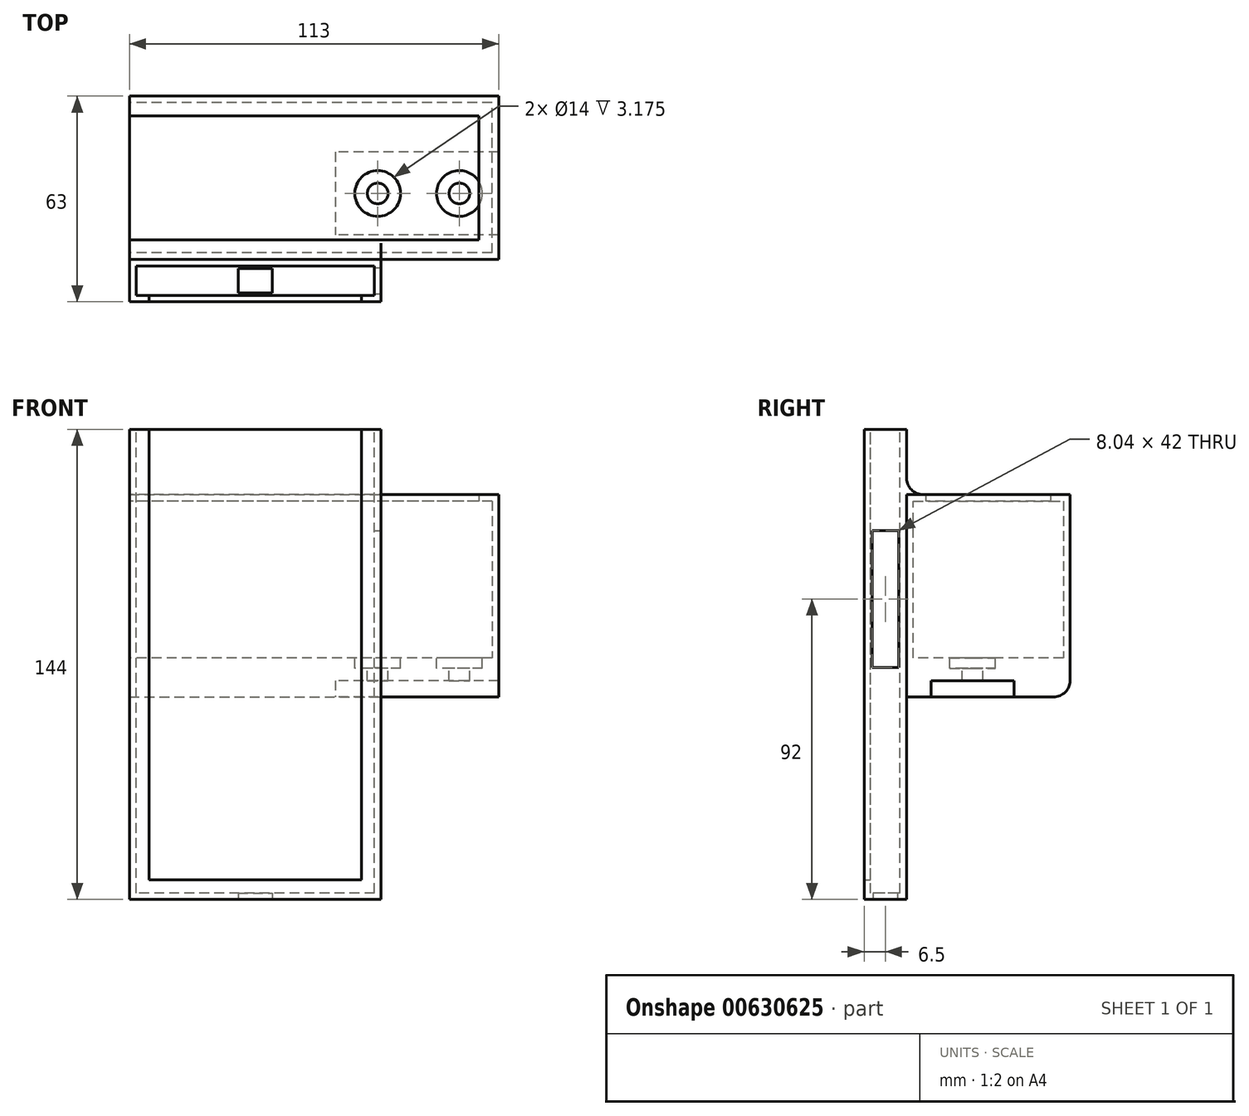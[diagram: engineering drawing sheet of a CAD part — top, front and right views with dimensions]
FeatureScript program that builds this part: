
annotation { "Feature Type Name" : "Feature", "Feature Type Description" : "" }
export const myFeature = defineFeature(function(context is Context, id is Id, definition is map)
    precondition{}
    {
        {
            var Q0;
            Q0=qCreatedBy(makeId("Front.planeOp"),FACE);
            var sketch = newSketch(context, id + "F0", { "sketchPlane" : qUnion([Q0])});
            skLineSegment(sketch, "E0.bottom", {"start": v(38.5, -72) * mm, "end": v(-38.5, -72) * mm});
            skLineSegment(sketch, "E0.top", {"start": v(38.5, 72) * mm, "end": v(-38.5, 72) * mm});
            skLineSegment(sketch, "E0.left", {"start": v(38.5, -72) * mm, "end": v(38.5, 72) * mm});
            skLineSegment(sketch, "E0.right", {"start": v(-38.5, -72) * mm, "end": v(-38.5, 72) * mm});
            skPoint(sketch, "E0.middle", {"position": v(0, 0) * mm});
            skSolve(sketch);
        }
        {
            var Q0;
            Q0=makeQuery(id+"F0.imprint","IMPRINT",FACE,{"disambiguationData":[TD([[makeQuery(id+"F0.imprint","IMPRINT",EDGE,{"derivedFrom":sQuery(id+"F0.wireOp",EDGE,"E0.bottom")}),-1.0]])]});
            extrude(context, id + "F1", {"entities" : qUnion([Q0]), "depth" : 13 * mm, "offsetDistance" : 25 * mm});
        }
        {
            var Q0;
            Q0=makeQuery(id+"F1.opExtrude","SWEPT_FACE",FACE,{"disambiguationData":[OSD([sQuery(id+"F0.wireOp",EDGE,"E0.top")])]});
            var sketch = newSketch(context, id + "F2", { "sketchPlane" : qUnion([Q0])});
            skLineSegment(sketch, "E1", {"start": v(-32.5, -13) * mm, "end": v(-32.5, -11) * mm});
            skLineSegment(sketch, "E2", {"start": v(-32.5, -11) * mm, "end": v(-36.5, -11) * mm});
            skLineSegment(sketch, "E3", {"start": v(-36.5, -11) * mm, "end": v(-36.5, -2) * mm});
            skLineSegment(sketch, "E4", {"start": v(-36.5, -2) * mm, "end": v(36.5, -2) * mm});
            skLineSegment(sketch, "E5", {"start": v(36.5, -2) * mm, "end": v(36.5, -11) * mm});
            skLineSegment(sketch, "E6", {"start": v(36.5, -11) * mm, "end": v(32.5, -11) * mm});
            skLineSegment(sketch, "E7", {"start": v(32.5, -11) * mm, "end": v(32.5, -13) * mm});
            skSolve(sketch);
        }
        {
            var Q0;
            {var subQ0=sQuery(id+"F2.wireOp",EDGE,"E1");Q0=makeQuery(id+"F2.imprint","IMPRINT",FACE,{"disambiguationData":[TD([[makeQuery(id+"F2.imprint","IMPRINT",EDGE,{"derivedFrom":subQ0}),-1.0]])]});}
            extrude(context, id + "F3", {"entities" : qUnion([Q0]), "operationType" : NewBodyOperationType.REMOVE, "oppositeDirection" : true, "depth" : 142 * mm, "offsetDistance" : 25 * mm});
        }
        {
            var Q0;
            Q0=makeQuery(id+"F3.boolean.opBoolean","COPY",FACE,{"derivedFrom":makeQuery(id+"F3.opExtrude","CAP_FACE",FACE,{"disambiguationData":[OSD([sQuery(id+"F0.wireOp",EDGE,"E0.top"),sQuery(id+"F2.wireOp",EDGE,"E1"),sQuery(id+"F2.wireOp",EDGE,"E2"),sQuery(id+"F2.wireOp",EDGE,"E3"),sQuery(id+"F2.wireOp",EDGE,"E4"),sQuery(id+"F2.wireOp",EDGE,"E5"),sQuery(id+"F2.wireOp",EDGE,"E6"),sQuery(id+"F2.wireOp",EDGE,"E7")])],"isStart":false})});
            var sketch = newSketch(context, id + "F4", { "sketchPlane" : qUnion([Q0])});
            skLineSegment(sketch, "E8", {"start": v(-32.5, -11) * mm, "end": v(32.5, -11) * mm});
            skSolve(sketch);
        }
        {
            var Q0;
            Q0=makeQuery(id+"F4.imprint","IMPRINT",FACE,{"disambiguationData":[TD([[makeQuery(id+"F4.imprint","IMPRINT",EDGE,{"derivedFrom":sQuery(id+"F4.wireOp",EDGE,"E8")}),-1.0]])]});
            extrude(context, id + "F5", {"entities" : qUnion([Q0]), "operationType" : NewBodyOperationType.ADD, "depth" : 4 * mm, "offsetDistance" : 25 * mm});
        }
        {
            var Q0;
            Q0=makeQuery(id+"F1.opExtrude","SWEPT_FACE",FACE,{"disambiguationData":[OSD([sQuery(id+"F0.wireOp",EDGE,"E0.bottom")])]});
            var sketch = newSketch(context, id + "F6", { "sketchPlane" : qUnion([Q0])});
            skPoint(sketch, "E9", {"position": v(0, 6.5) * mm});
            skLineSegment(sketch, "E10.bottom", {"start": v(5.25, 10.25) * mm, "end": v(-5.25, 10.25) * mm});
            skLineSegment(sketch, "E10.top", {"start": v(5.25, 2.75) * mm, "end": v(-5.25, 2.75) * mm});
            skLineSegment(sketch, "E10.left", {"start": v(5.25, 10.25) * mm, "end": v(5.25, 2.75) * mm});
            skLineSegment(sketch, "E10.right", {"start": v(-5.25, 10.25) * mm, "end": v(-5.25, 2.75) * mm});
            skSolve(sketch);
        }
        {
            var Q0;
            Q0=makeQuery(id+"F6.imprint","IMPRINT",FACE,{"disambiguationData":[TD([[makeQuery(id+"F6.imprint","IMPRINT",EDGE,{"derivedFrom":sQuery(id+"F6.wireOp",EDGE,"E10.bottom")}),1.0]])]});
            extrude(context, id + "F7", {"entities" : qUnion([Q0]), "operationType" : NewBodyOperationType.REMOVE, "oppositeDirection" : true, "depth" : 25 * mm, "offsetDistance" : 25 * mm});
        }
        {
            var Q0;
            Q0=makeQuery(id+"F1.opExtrude","SWEPT_FACE",FACE,{"disambiguationData":[OSD([sQuery(id+"F0.wireOp",EDGE,"E0.left")])]});
            var sketch = newSketch(context, id + "F8", { "sketchPlane" : qUnion([Q0])});
            skPoint(sketch, "E11", {"position": v(-6.5, 20) * mm});
            skLineSegment(sketch, "E12.bottom", {"start": v(-2.48, 41) * mm, "end": v(-10.52, 41) * mm});
            skLineSegment(sketch, "E12.top", {"start": v(-2.48, -1) * mm, "end": v(-10.52, -1) * mm});
            skLineSegment(sketch, "E12.left", {"start": v(-2.48, 41) * mm, "end": v(-2.48, -1) * mm});
            skLineSegment(sketch, "E12.right", {"start": v(-10.52, 41) * mm, "end": v(-10.52, -1) * mm});
            skSolve(sketch);
        }
        {
            var Q0;
            Q0=makeQuery(id+"F8.imprint","IMPRINT",FACE,{"disambiguationData":[TD([[makeQuery(id+"F8.imprint","IMPRINT",EDGE,{"derivedFrom":sQuery(id+"F8.wireOp",EDGE,"E12.bottom")}),1.0]])]});
            extrude(context, id + "F9", {"entities" : qUnion([Q0]), "operationType" : NewBodyOperationType.REMOVE, "oppositeDirection" : true, "depth" : 25 * mm, "offsetDistance" : 25 * mm});
        }
        {
            var Q0;
            Q0=makeQuery(id+"F1.opExtrude","CAP_FACE",FACE,{"disambiguationData":[OSD([sQuery(id+"F0.wireOp",EDGE,"E0.bottom"),sQuery(id+"F0.wireOp",EDGE,"E0.top"),sQuery(id+"F0.wireOp",EDGE,"E0.left"),sQuery(id+"F0.wireOp",EDGE,"E0.right")])],"isStart":true});
            var sketch = newSketch(context, id + "F10", { "sketchPlane" : qUnion([Q0])});
            skLineSegment(sketch, "E13.bottom", {"start": v(38.5, 52) * mm, "end": v(-74.5, 52) * mm});
            skLineSegment(sketch, "E13.top", {"start": v(38.5, -2) * mm, "end": v(-74.5, -2) * mm});
            skLineSegment(sketch, "E13.left", {"start": v(38.5, 52) * mm, "end": v(38.5, -2) * mm});
            skLineSegment(sketch, "E13.right", {"start": v(-74.5, 52) * mm, "end": v(-74.5, -2) * mm});
            skSolve(sketch);
        }
        {
            var Q0;
            {var subQ0=sQuery(id+"F10.wireOp",EDGE,"E13.left");Q0=makeQuery(id+"F10.imprint","IMPRINT",FACE,{"disambiguationData":[TD([[makeQuery(id+"F10.imprint","IMPRINT",EDGE,{"derivedFrom":subQ0}),1.0]])]});}
            var Q1;
            {var subQ0=sQuery(id+"F10.wireOp",EDGE,"E13.right");Q1=makeQuery(id+"F10.imprint","IMPRINT",FACE,{"disambiguationData":[TD([[makeQuery(id+"F10.imprint","IMPRINT",EDGE,{"derivedFrom":subQ0}),1.0]])]});}
            extrude(context, id + "F11", {"entities" : qUnion([Q0, Q1]), "operationType" : NewBodyOperationType.ADD, "depth" : 50 * mm, "offsetDistance" : 25 * mm});
        }
        {
            var Q0;
            Q0=makeQuery(id+"F11.boolean.opBoolean","MERGE",FACE,{"derivedFrom":[makeQuery(id+"F1.opExtrude","SWEPT_FACE",FACE,{"disambiguationData":[OSD([sQuery(id+"F0.wireOp",EDGE,"E0.right")])]}),makeQuery(id+"F11.opExtrude","SWEPT_FACE",FACE,{"disambiguationData":[OSD([sQuery(id+"F10.wireOp",EDGE,"E13.left")])]})]});
            var sketch = newSketch(context, id + "F12", { "sketchPlane" : qUnion([Q0])});
            skLineSegment(sketch, "E14", {"start": v(0, 52) * mm, "end": v(0, -2) * mm});
            skLineSegment(sketch, "E15", {"start": v(-44, 52) * mm, "end": v(-44, 50) * mm});
            skLineSegment(sketch, "E16", {"start": v(-44, 50) * mm, "end": v(-48, 50) * mm});
            skLineSegment(sketch, "E17", {"start": v(-48, 50) * mm, "end": v(-48, 2) * mm});
            skLineSegment(sketch, "E18", {"start": v(-48, 2) * mm, "end": v(-2, 2) * mm});
            skLineSegment(sketch, "E19", {"start": v(-2, 2) * mm, "end": v(-2, 50) * mm});
            skLineSegment(sketch, "E20", {"start": v(-2, 50) * mm, "end": v(-6, 50) * mm});
            skLineSegment(sketch, "E21", {"start": v(-6, 50) * mm, "end": v(-6, 52) * mm});
            skSolve(sketch);
        }
        {
            var Q0;
            {var subQ0=sQuery(id+"F12.wireOp",EDGE,"E15");Q0=makeQuery(id+"F12.imprint","IMPRINT",FACE,{"disambiguationData":[TD([[makeQuery(id+"F12.imprint","IMPRINT",EDGE,{"derivedFrom":subQ0}),1.0]])]});}
            extrude(context, id + "F13", {"entities" : qUnion([Q0]), "operationType" : NewBodyOperationType.REMOVE, "oppositeDirection" : true, "depth" : 111 * mm, "offsetDistance" : 25 * mm});
        }
        {
            var Q0;
            Q0=makeQuery(id+"F13.boolean.opBoolean","COPY",FACE,{"derivedFrom":makeQuery(id+"F13.opExtrude","CAP_FACE",FACE,{"disambiguationData":[OSD([sQuery(id+"F0.wireOp",EDGE,"E0.right"),sQuery(id+"F10.wireOp",EDGE,"E13.bottom"),sQuery(id+"F10.wireOp",EDGE,"E13.left"),sQuery(id+"F12.wireOp",EDGE,"E15"),sQuery(id+"F12.wireOp",EDGE,"E16"),sQuery(id+"F12.wireOp",EDGE,"E17"),sQuery(id+"F12.wireOp",EDGE,"E18"),sQuery(id+"F12.wireOp",EDGE,"E19"),sQuery(id+"F12.wireOp",EDGE,"E20"),sQuery(id+"F12.wireOp",EDGE,"E21")])],"isStart":false})});
            var sketch = newSketch(context, id + "F14", { "sketchPlane" : qUnion([Q0])});
            skLineSegment(sketch, "E22", {"start": v(-44, 50) * mm, "end": v(-6, 50) * mm});
            skSolve(sketch);
        }
        {
            var Q0;
            Q0 = qSketchRegion(id + "F14", true);
            var Q1;
            Q1=makeQuery(id+"F14.imprint","IMPRINT",FACE,{"disambiguationData":[TD([[makeQuery(id+"F14.imprint","IMPRINT",EDGE,{"derivedFrom":sQuery(id+"F14.wireOp",EDGE,"E22")}),1.0]])]});
            extrude(context, id + "F15", {"entities" : qUnion([Q0, Q1]), "operationType" : NewBodyOperationType.ADD, "depth" : 4 * mm, "offsetDistance" : 25 * mm});
        }
        {
            var Q0;
            Q0=makeQuery(id+"F11.opExtrude","SWEPT_FACE",FACE,{"disambiguationData":[OSD([sQuery(id+"F10.wireOp",EDGE,"E13.top")])]});
            extrude(context, id + "F16", {"entities" : qUnion([Q0]), "operationType" : NewBodyOperationType.ADD, "depth" : 8 * mm, "offsetDistance" : 25 * mm});
        }
        {
            var Q0;
            Q0=makeQuery(id+"F16.opExtrude","CAP_FACE",FACE,{"disambiguationData":[OSD([sQuery(id+"F10.wireOp",EDGE,"E13.top")])],"isStart":false});
            var sketch = newSketch(context, id + "F17", { "sketchPlane" : qUnion([Q0])});
            skLineSegment(sketch, "E23.bottom", {"start": v(74.5, -32.9) * mm, "end": v(24.5, -32.9) * mm});
            skLineSegment(sketch, "E23.top", {"start": v(74.5, -7.5) * mm, "end": v(24.5, -7.5) * mm});
            skLineSegment(sketch, "E23.left", {"start": v(74.5, -32.9) * mm, "end": v(74.5, -7.5) * mm});
            skLineSegment(sketch, "E23.right", {"start": v(24.5, -32.9) * mm, "end": v(24.5, -7.5) * mm});
            skSolve(sketch);
        }
        {
            var Q0;
            Q0=makeQuery(id+"F17.imprint","IMPRINT",FACE,{"disambiguationData":[TD([[makeQuery(id+"F17.imprint","IMPRINT",EDGE,{"derivedFrom":sQuery(id+"F17.wireOp",EDGE,"E23.bottom")}),-1.0]])]});
            extrude(context, id + "F18", {"entities" : qUnion([Q0]), "operationType" : NewBodyOperationType.REMOVE, "oppositeDirection" : true, "depth" : 5 * mm, "offsetDistance" : 25 * mm});
        }
        {
            var Q0;
            Q0=makeQuery(id+"F13.boolean.opBoolean","COPY",FACE,{"derivedFrom":makeQuery(id+"F13.opExtrude","SWEPT_FACE",FACE,{"disambiguationData":[OSD([sQuery(id+"F12.wireOp",EDGE,"E18")])]})});
            var sketch = newSketch(context, id + "F19", { "sketchPlane" : qUnion([Q0])});
            skPoint(sketch, "E24", {"position": v(62.5, 20.2) * mm});
            skPoint(sketch, "E25", {"position": v(37.5, 20.2) * mm});
            skSolve(sketch);
        }
        {
            var Q0;
            Q0=sQuery(id+"F19.wireOp",VERTEX,"E24");
            var Q1;
            Q1=sQuery(id+"F19.wireOp",VERTEX,"E25");
            var Q2;
            Q2=makeQuery(id+"F1.opExtrude","SWEPT_BODY",BODY,{"disambiguationData":[OSD([sQuery(id+"F0.wireOp",EDGE,"E0.bottom"),sQuery(id+"F0.wireOp",EDGE,"E0.top"),sQuery(id+"F0.wireOp",EDGE,"E0.left"),sQuery(id+"F0.wireOp",EDGE,"E0.right")])]});
            hole(context, id + "F20", {"style" : HoleStyle.C_BORE, "endStyle" : HoleEndStyle.BLIND, "holeDiameter" : 6.35 * mm, "cBoreDiameter" : 14 * mm, "cBoreDepth" : 3.17 * mm, "majorDiameter" : 5 * mm, "holeDepth" : 8 * mm, "isTappedThrough" : true, "tappedDepth" : 12 * mm, "tapClearance" : 3, "locations" : qUnion([Q0, Q1]), "scope" : qUnion([Q2])});
        }
        {
            var Q0;
            {var subQ0=makeQuery(id+"F1.opExtrude","CAP_FACE",FACE,{"disambiguationData":[OSD([sQuery(id+"F0.wireOp",EDGE,"E0.bottom"),sQuery(id+"F0.wireOp",EDGE,"E0.top"),sQuery(id+"F0.wireOp",EDGE,"E0.left"),sQuery(id+"F0.wireOp",EDGE,"E0.right")])],"isStart":true});var subQ1=sQuery(id+"F10.wireOp",EDGE,"E13.top");var subQ3=makeQuery(id+"F11.opExtrude","CAP_EDGE",EDGE,{"disambiguationData":[OSD([subQ1])],"isStart":true});Q0=makeQuery(id+"F16.boolean.opBoolean","SPLIT",EDGE,{"disambiguationData":[topologyDisambiguationEdgeConnected([subQ0])],"derivedFrom":makeQuery(id+"F16.opExtrude","CAP_EDGE",EDGE,{"disambiguationData":[OSD([subQ1]),TDD([makeQuery(id+"F11.boolean.opBoolean","SPLIT",EDGE,{"disambiguationData":[topologyDisambiguationEdgeConnected([makeQuery(id+"F11.opExtrude","CAP_FACE",FACE,{"disambiguationData":[OSD([sQuery(id+"F10.wireOp",EDGE,"E13.bottom"),subQ1,sQuery(id+"F10.wireOp",EDGE,"E13.left"),sQuery(id+"F10.wireOp",EDGE,"E13.right")])],"isStart":true})])],"derivedFrom":subQ3}),makeQuery(id+"F11.boolean.opBoolean","SPLIT",EDGE,{"disambiguationData":[topologyDisambiguationEdgeConnected([subQ0])],"derivedFrom":subQ3})])],"isStart":false})});}
            var Q1;
            {var subQ0=sQuery(id+"F10.wireOp",EDGE,"E13.bottom");Q1=makeQuery(id+"F11.boolean.opBoolean","SPLIT",EDGE,{"disambiguationData":[topologyDisambiguationEdgeConnected([makeQuery(id+"F1.opExtrude","CAP_FACE",FACE,{"disambiguationData":[OSD([sQuery(id+"F0.wireOp",EDGE,"E0.bottom"),sQuery(id+"F0.wireOp",EDGE,"E0.top"),sQuery(id+"F0.wireOp",EDGE,"E0.left"),sQuery(id+"F0.wireOp",EDGE,"E0.right")])],"isStart":true})])],"derivedFrom":makeQuery(id+"F11.opExtrude","CAP_EDGE",EDGE,{"disambiguationData":[OSD([subQ0])],"isStart":true})});}
            fillet(context, id + "F21", {"entities" : qUnion([Q0, Q1]), "radius" : 5 * mm, "tangentPropagation" : true, "allowEdgeOverflow" : false});
        }
    });
